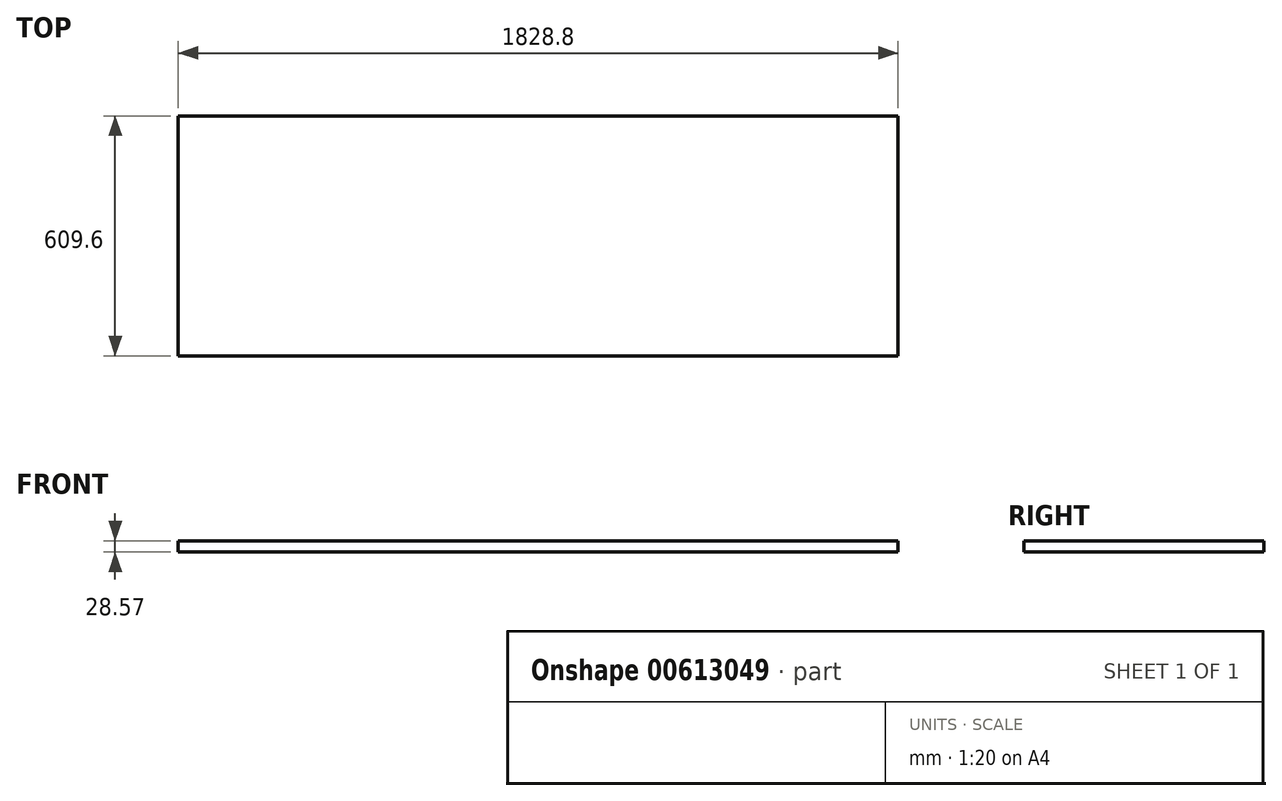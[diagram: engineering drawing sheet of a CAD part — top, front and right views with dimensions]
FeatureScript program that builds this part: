
annotation { "Feature Type Name" : "Feature", "Feature Type Description" : "" }
export const myFeature = defineFeature(function(context is Context, id is Id, definition is map)
    precondition{}
    {
        {
            var Q0;
            Q0=qCreatedBy(makeId("Top.planeOp"),FACE);
            var sketch = newSketch(context, id + "F0", { "sketchPlane" : qUnion([Q0])});
            skLineSegment(sketch, "E0.bottom", {"start": v(914.4, 304.8) * mm, "end": v(-914.4, 304.8) * mm});
            skLineSegment(sketch, "E0.top", {"start": v(914.4, -304.8) * mm, "end": v(-914.4, -304.8) * mm});
            skLineSegment(sketch, "E0.left", {"start": v(914.4, 304.8) * mm, "end": v(914.4, -304.8) * mm});
            skLineSegment(sketch, "E0.right", {"start": v(-914.4, 304.8) * mm, "end": v(-914.4, -304.8) * mm});
            skPoint(sketch, "E0.middle", {"position": v(0, 0) * mm});
            skSolve(sketch);
        }
        {
            var Q0;
            Q0=makeQuery(id+"F0.imprint","IMPRINT",FACE,{"disambiguationData":[TD([[makeQuery(id+"F0.imprint","IMPRINT",EDGE,{"derivedFrom":sQuery(id+"F0.wireOp",EDGE,"E0.bottom")}),1.0]])]});
            extrude(context, id + "F1", {"entities" : qUnion([Q0]), "depth" : 28.57 * mm, "offsetDistance" : 25.4 * mm});
        }
    });
